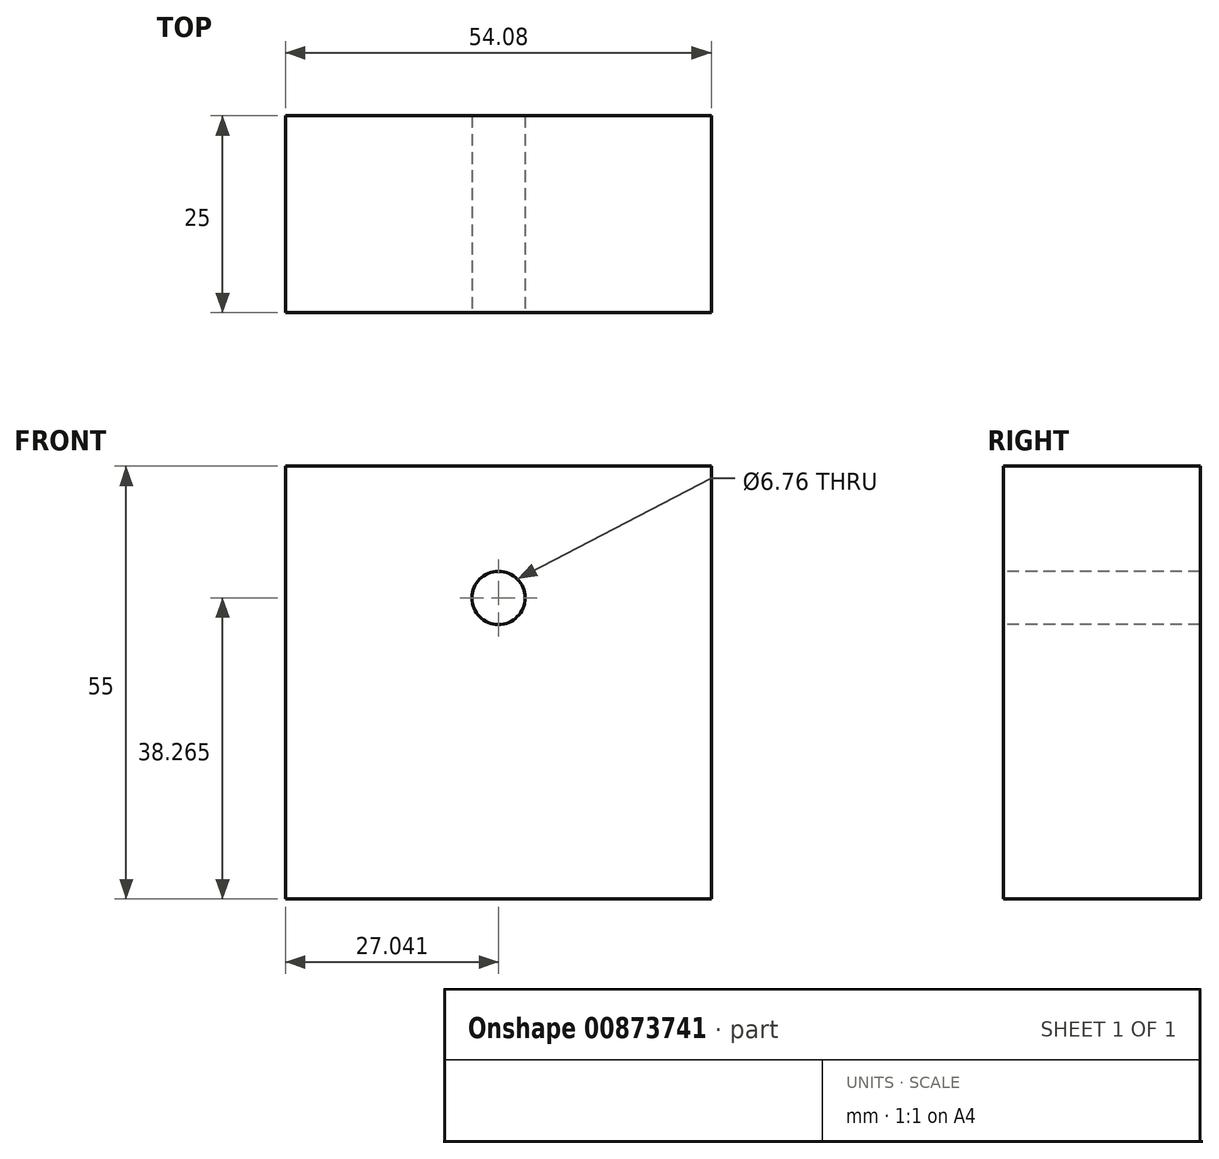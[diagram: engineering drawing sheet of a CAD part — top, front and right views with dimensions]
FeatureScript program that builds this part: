
annotation { "Feature Type Name" : "Feature", "Feature Type Description" : "" }
export const myFeature = defineFeature(function(context is Context, id is Id, definition is map)
    precondition{}
    {
        {
            var Q0;
            Q0=qCreatedBy(makeId("Front.planeOp"),FACE);
            var sketch = newSketch(context, id + "F0", { "sketchPlane" : qUnion([Q0])});
            skLineSegment(sketch, "E0.bottom", {"start": v(-121.67, -10.59) * mm, "end": v(-67.6, -10.59) * mm});
            skLineSegment(sketch, "E0.top", {"start": v(-121.67, 44.4) * mm, "end": v(-67.6, 44.4) * mm});
            skLineSegment(sketch, "E0.left", {"start": v(-121.67, -10.59) * mm, "end": v(-121.67, 44.4) * mm});
            skLineSegment(sketch, "E0.right", {"start": v(-67.6, -10.59) * mm, "end": v(-67.6, 44.4) * mm});
            skPoint(sketch, "E0.middle", {"position": v(-94.63, 16.9) * mm});
            skSolve(sketch);
        }
        {
            var Q0;
            Q0=makeQuery(id+"F0.imprint","IMPRINT",FACE,{"disambiguationData":[TD([[makeQuery(id+"F0.imprint","IMPRINT",EDGE,{"derivedFrom":sQuery(id+"F0.wireOp",EDGE,"E0.bottom")}),1.0]])]});
            extrude(context, id + "F1", {"entities" : qUnion([Q0]), "depth" : 25 * mm, "offsetDistance" : 25 * mm});
        }
        {
            var Q0;
            Q0=makeQuery(id+"F1.opExtrude","CAP_FACE",FACE,{"disambiguationData":[OSD([sQuery(id+"F0.wireOp",EDGE,"E0.bottom"),sQuery(id+"F0.wireOp",EDGE,"E0.top"),sQuery(id+"F0.wireOp",EDGE,"E0.left"),sQuery(id+"F0.wireOp",EDGE,"E0.right")])],"isStart":false});
            var sketch = newSketch(context, id + "F2", { "sketchPlane" : qUnion([Q0])});
            skPoint(sketch, "E1", {"position": v(-94.63, 27.67) * mm});
            skPoint(sketch, "E1.positionSnap0", {"position": v(-94.63, -10.59) * mm});
            skSolve(sketch);
        }
        {
            var Q0;
            Q0=sQuery(id+"F2.wireOp",VERTEX,"E1");
            var Q1;
            Q1=makeQuery(id+"F1.opExtrude","SWEPT_BODY",BODY,{"disambiguationData":[OSD([sQuery(id+"F0.wireOp",EDGE,"E0.bottom"),sQuery(id+"F0.wireOp",EDGE,"E0.top"),sQuery(id+"F0.wireOp",EDGE,"E0.left"),sQuery(id+"F0.wireOp",EDGE,"E0.right")])]});
            hole(context, id + "F3", {"style" : HoleStyle.SIMPLE, "endStyle" : HoleEndStyle.THROUGH, "standardTappedOrClearance" : lookupTablePath({ "fit" : "Normal (ASME)", "standard" : "ANSI", "size" : "1/4", "type" : "Clearance" }), "standardBlindInLast" : lookupTablePath({ "fit" : "Free", "standard" : "ANSI", "size" : "1/4", "type" : "Clearance" }), "holeDiameter" : 6.76 * mm, "majorDiameter" : 5 * mm, "isTappedThrough" : true, "tappedDepth" : 12 * mm, "tapClearance" : 3, "locations" : qUnion([Q0]), "scope" : qUnion([Q1])});
        }
    });
